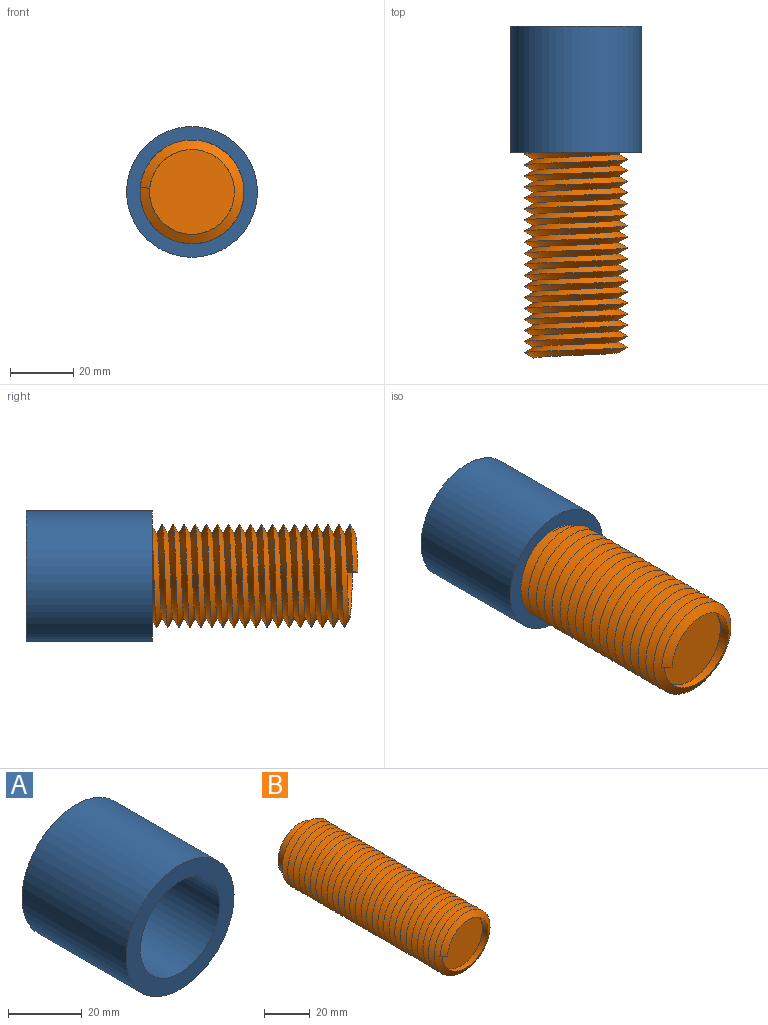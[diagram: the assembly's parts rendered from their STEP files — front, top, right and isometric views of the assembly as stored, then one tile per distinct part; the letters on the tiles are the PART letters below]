
ASSEMBLY  parts=2 mates=1
PART A: 4 faces, bbox 41.4x40x41.4 mm
  f0: cylinder r=15.25mm len=40mm, axis (0,1,0), area 3832.7mm2, adj f2,f3
  f1: cylinder r=20.71mm len=41.42mm, axis (0,1,0), area 5204.7mm2, adj f2,f3
  f2: plane 41.42x41.42mm, normal (0,-1,0), area 616.7mm2, adj f0,f1
  f3: plane 41.42x41.42mm, normal (0,1,0), area 616.7mm2, adj f0,f1
PART B: 35 faces, bbox 34.4x105.2x37.8 mm
  f0: cylinder r=13.48mm len=26.97mm, axis (0,1,0), area 300.6mm2, adj f27,f29,f30,f33,f34
  f1: cylinder r=13.48mm len=26.97mm, axis (0,1,0), area 13.1mm2, adj f2,f28,f33,f34
  f2: cylinder r=13.48mm len=26.97mm, axis (0,1,0), area 13.4mm2, adj f1,f3,f33,f34
  f3: cylinder r=13.48mm len=26.97mm, axis (0,1,0), area 13.5mm2, adj f2,f4,f33,f34
  f4: cylinder r=13.48mm len=26.97mm, axis (0,1,0), area 13.5mm2, adj f3,f5,f33,f34
  f5: cylinder r=13.48mm len=26.97mm, axis (0,1,0), area 13.4mm2, adj f4,f6,f33,f34
  f6: cylinder r=13.48mm len=26.97mm, axis (0,1,0), area 13.5mm2, adj f5,f7,f33,f34
  f7: cylinder r=13.48mm len=26.97mm, axis (0,1,0), area 13.5mm2, adj f6,f8,f33,f34
  f8: cylinder r=13.48mm len=26.97mm, axis (0,1,0), area 13.4mm2, adj f7,f9,f33,f34
  f9: cylinder r=13.48mm len=26.97mm, axis (0,1,0), area 13.5mm2, adj f8,f10,f33,f34
  f10: cylinder r=13.48mm len=26.97mm, axis (0,1,0), area 13.5mm2, adj f9,f11,f33,f34
  f11: cylinder r=13.48mm len=26.97mm, axis (0,1,0), area 13.4mm2, adj f10,f12,f33,f34
  f12: cylinder r=13.48mm len=26.97mm, axis (0,1,0), area 13.4mm2, adj f11,f13,f33,f34
  f13: cylinder r=13.48mm len=26.97mm, axis (0,1,0), area 13.4mm2, adj f12,f14,f33,f34
  f14: cylinder r=13.48mm len=26.97mm, axis (0,1,0), area 13.4mm2, adj f13,f15,f33,f34
  f15: cylinder r=13.48mm len=26.97mm, axis (0,1,0), area 13.4mm2, adj f14,f16,f33,f34
  f16: cylinder r=13.48mm len=26.97mm, axis (0,1,0), area 13.4mm2, adj f15,f17,f33,f34
  f17: cylinder r=13.48mm len=26.97mm, axis (0,1,0), area 13.3mm2, adj f16,f18,f33,f34
  f18: cylinder r=13.48mm len=26.97mm, axis (0,1,0), area 13.4mm2, adj f17,f19,f33,f34
  f19: cylinder r=13.48mm len=26.97mm, axis (0,1,0), area 13.4mm2, adj f18,f20,f33,f34
  f20: cylinder r=13.48mm len=26.97mm, axis (0,1,0), area 13.3mm2, adj f19,f21,f33,f34
  f21: cylinder r=13.48mm len=26.97mm, axis (0,1,0), area 13.4mm2, adj f20,f22,f33,f34
  f22: cylinder r=13.48mm len=26.97mm, axis (0,1,0), area 13.4mm2, adj f21,f23,f33,f34
  f23: cylinder r=13.48mm len=26.97mm, axis (0,1,0), area 13.3mm2, adj f22,f24,f33,f34
  f24: cylinder r=13.48mm len=26.97mm, axis (0,1,0), area 13.4mm2, adj f23,f25,f33,f34
  f25: cylinder r=13.48mm len=26.97mm, axis (0,1,0), area 13.4mm2, adj f24,f26,f33,f34
  f26: cylinder r=13.48mm len=26.97mm, axis (0,1,0), area 13.3mm2, adj f25,f27,f33,f34
  f27: cylinder r=13.48mm len=26.97mm, axis (0,1,0), area 13.4mm2, adj f0,f26,f33,f34
  f28: plane 26.92x26.87mm, normal (0,-1,0), area 567.1mm2, adj f1,f32,f33,f34
  f29: plane 26.97x26.97mm, normal (0,1,0), area 571.2mm2, adj f0
  f30: plane 3.35x2.54mm, normal (-0.51,0,-0.86), area 4.9mm2, adj f0,f33,f34
  f31: plane 3.4x2.99mm, normal (-0.09,0,-1), area 5.1mm2, adj f32,f33,f34
  f32: cylinder r=13.43mm len=26.87mm, axis (0,1,0), area 283mm2, adj f28,f31,f33,f34
  f33: bspline ~102.03x37.81mm, area 9114.6mm2, adj f0,f1,f2,f3,f4,f5,f6,f7
  f34: bspline ~102.03x37.81mm, area 9114.2mm2, adj f0,f1,f2,f3,f4,f5,f6,f7
PLACE A t=(-1.1,23.4,0)mm
PLACE B t=(-1.1,43.4,0)mm
MATE cylindrical B.f0 <-> A.f0  axis (0,1,0) through (-1.1,43.4,0)mm
